# Revit family: NaughtOne_HatchTwoSeatBenchWork
name_source: partatom
category: Furniture
units: mm (PartAtom-declared; Revit-internal decimal feet)

## family parameters
Always vertical = Yes
Cut with Voids When Loaded = No
Enable Cutting in Views = No
Render Appearance Source = Family Geometry
Room Calculation Point = No
Shared = Yes
Work Plane-Based = No

## types (1)
- Work height 18 inch seat height Single Fabric
    Assembly Code = E2020200
    AssetType = Movable
    BIMObjectName = Naughtone_Seating_Hatch_Bench
    Category = Pr_40_50_12_07: Benches
    CodePerformance = PASSED BSEN 16139
    Color = Various
    Default Elevation = 0 "
    Description = Hatch Two Seat Bench Work height 18 inch seat height Single Fabric
    DurationUnit = year
    Export Type to IFC As = IfcFurnishingElementType
    Finish = Upholstered
    IfcExportAs = IfcFurnishingElementType
    IfcExportType = BENCH
    Is2Seat = Yes
    Is3Seat = No
    IsChair = Yes
    LeftOffset = 20 "
    MainColor = Various
    Manufacturer = naughtone
    ManufacturerAddressUK = naughtone, Knaresborough Tech Park, Manse Lane, Knaresborough, HG5 8LF
    ManufacturerName = Naughtone
    ManufacturerURL = www.naughtone.com
    Material = Fabric, leather/steel/solid wood/beech ply/foam
    Model = NOHAN210W1
    ModelNumber = HAT2BEN
    ModelReference = Hatch 2 Seat Bench
    NBSDescription = Seating
    NBSReference = 45-35-72/352
    Name = Seating_Hatch_Bench_Naughtone
    NominalHeight = 16 "
    NominalLength = 40 "
    NominalWidth = 20 "
    Package Qty = 1
    Product Documentation Link = http://www.naughtone.com
    ProductInformation = www.naughtone.com/portfolio-view/hatch
    RightOffset = 20 "
    Shape = Rectangular
    Size = 1020x510x410mm
    SustainabilityPerformance = FSC certified. FISP certified. ISO 14001 certified
    Type IFC Predefined Type = BENCH
    URL = http://www.hermanmiller.com
    Uniclass2015Description = Benches
    Uniclass2015Reference = Pr_40_50_12_07
    Uniclass2015Version = Products v1.5
    Version = 1
    VoidOffset2Seat = 0 "
    VoidOffset3Seat = 0 "
    VoidOffsetCentre = 0 "
    WarrantyDurationLabor = 5
    WarrantyDurationParts = 5
    WarrantyDurationUnit = year

## geometry (parser evidence)
native form markers: Sweep x4
no freeform markers — native parametric forms only
